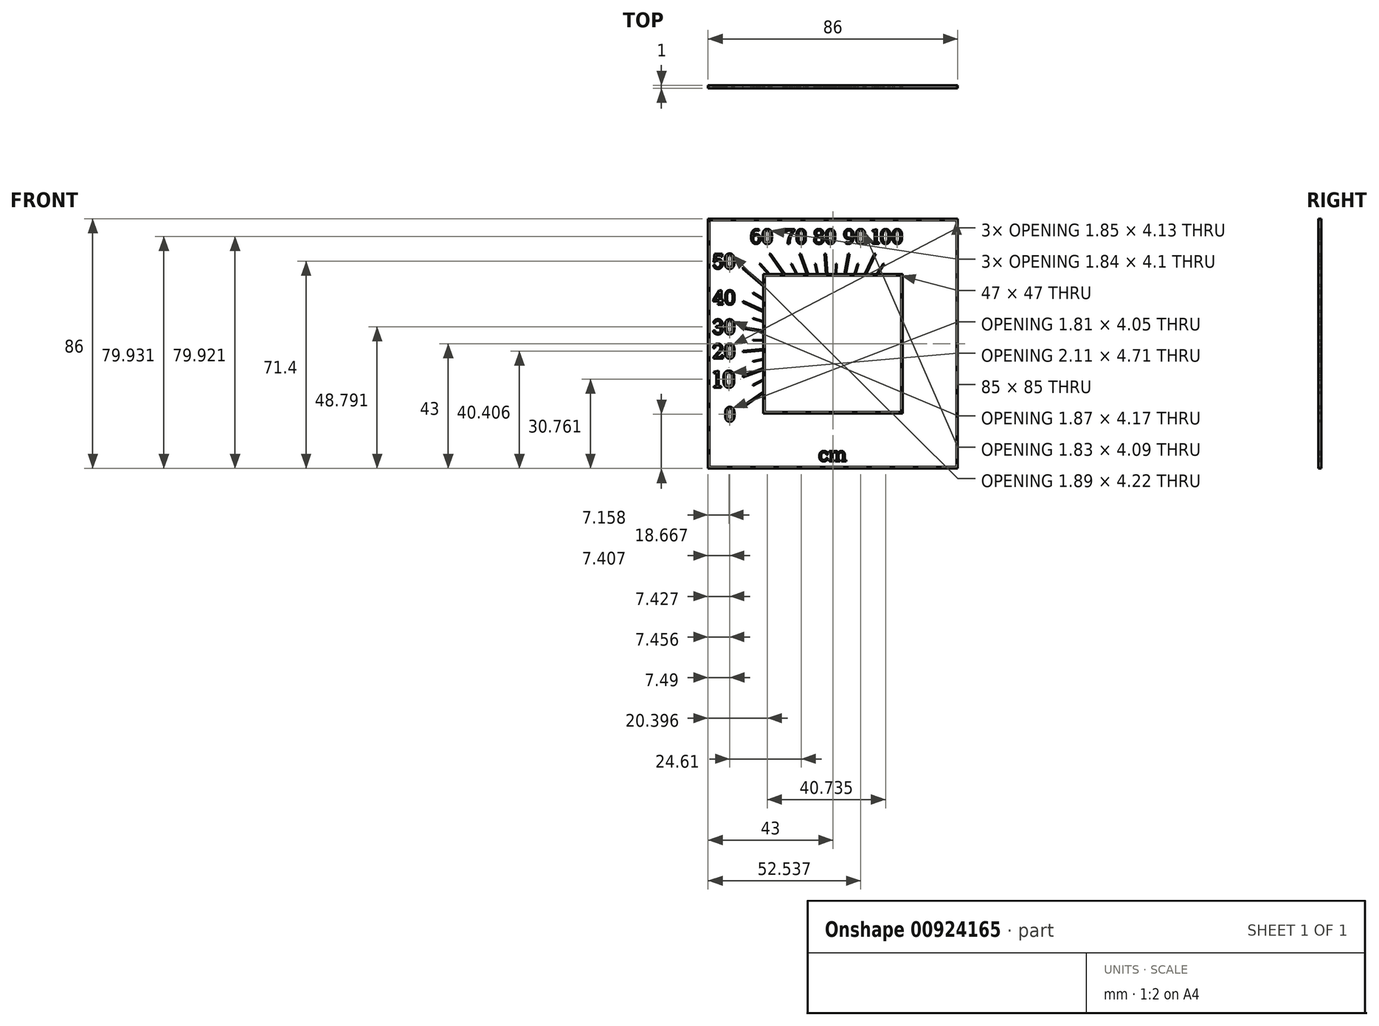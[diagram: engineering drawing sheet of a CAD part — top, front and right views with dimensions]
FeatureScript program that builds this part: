
annotation { "Feature Type Name" : "Feature", "Feature Type Description" : "" }
export const myFeature = defineFeature(function(context is Context, id is Id, definition is map)
    precondition{}
    {
        {
            var Q0;
            Q0=qCreatedBy(makeId("Front.planeOp"),FACE);
            var sketch = newSketch(context, id + "F0", { "sketchPlane" : qUnion([Q0])});
            skLineSegment(sketch, "E0.bottom", {"start": v(-24, 24) * mm, "end": v(-16.8, 24) * mm});
            skLineSegment(sketch, "E0.top", {"start": v(-24, -24) * mm, "end": v(24, -24) * mm});
            skLineSegment(sketch, "E0.left", {"start": v(-24, 24) * mm, "end": v(-24, 11.13) * mm});
            skLineSegment(sketch, "E0.right", {"start": v(24, 24) * mm, "end": v(24, -24) * mm});
            skLineSegment(sketch, "E1.bottom", {"start": v(42.5, -42.5) * mm, "end": v(-42.5, -42.5) * mm});
            skLineSegment(sketch, "E1.top", {"start": v(42.5, 42.5) * mm, "end": v(-42.5, 42.5) * mm});
            skLineSegment(sketch, "E1.left", {"start": v(42.5, -42.5) * mm, "end": v(42.5, 42.5) * mm});
            skLineSegment(sketch, "E1.right", {"start": v(-42.5, -42.5) * mm, "end": v(-42.5, 42.5) * mm});
            skPoint(sketch, "E1.middle", {"position": v(0, 0) * mm});
            skLineSegment(sketch, "E2", {"start": v(0, 0) * mm, "end": v(-29, -20.3) * mm});
            skLineSegment(sketch, "E3.1.0", {"start": v(0, 0) * mm, "end": v(-24, -8.74) * mm, "construction": true});
            skLineSegment(sketch, "E3.2.0", {"start": v(0, 0) * mm, "end": v(-24, -2.1) * mm, "construction": true});
            skLineSegment(sketch, "E3.3.0", {"start": v(0, 0) * mm, "end": v(-24, 4.23) * mm, "construction": true});
            skLineSegment(sketch, "E3.4.0", {"start": v(0, 0) * mm, "end": v(-24, 11.2) * mm, "construction": true});
            skLineSegment(sketch, "E3.5.0", {"start": v(0, 0) * mm, "end": v(-24, 20.14) * mm, "construction": true});
            skLineSegment(sketch, "E3.6.0", {"start": v(0, 0) * mm, "end": v(-20.3, 29) * mm});
            skLineSegment(sketch, "E3.7.0", {"start": v(0, 0) * mm, "end": v(-8.74, 24) * mm, "construction": true});
            skLineSegment(sketch, "E3.8.0", {"start": v(0, 0) * mm, "end": v(-2.1, 24) * mm, "construction": true});
            skLineSegment(sketch, "E3.9.0", {"start": v(0, 0) * mm, "end": v(4.23, 24) * mm, "construction": true});
            skLineSegment(sketch, "E3.10.0", {"start": v(0, 0) * mm, "end": v(14.46, 31) * mm});
            skLineSegment(sketch, "E3.anchor1", {"start": v(0, 0) * mm, "end": v(-24, -16.8) * mm, "construction": true});
            skLineSegment(sketch, "E3.anchor2", {"start": v(0, 0) * mm, "end": v(11.2, 24) * mm, "construction": true});
            skText(sketch, "E4", { "text": "0", "fontName": "RobotoSlab-Regular.ttf"});
            skText(sketch, "E5", { "text": "10", "fontName": "RobotoSlab-Regular.ttf"});
            skText(sketch, "E6", { "text": "20", "fontName": "RobotoSlab-Regular.ttf"});
            skText(sketch, "E7", { "text": "30", "fontName": "RobotoSlab-Regular.ttf"});
            skText(sketch, "E8", { "text": "40", "fontName": "RobotoSlab-Regular.ttf"});
            skText(sketch, "E9", { "text": "50", "fontName": "RobotoSlab-Regular.ttf"});
            skText(sketch, "E10", { "text": "60", "fontName": "RobotoSlab-Regular.ttf"});
            skText(sketch, "E11", { "text": "70", "fontName": "RobotoSlab-Regular.ttf"});
            skText(sketch, "E12", { "text": "80", "fontName": "RobotoSlab-Regular.ttf"});
            skText(sketch, "E13", { "text": "90", "fontName": "RobotoSlab-Regular.ttf"});
            skText(sketch, "E14", { "text": "100", "fontName": "RobotoSlab-Regular.ttf"});
            skLineSegment(sketch, "E15", {"start": v(-41.5, 33.62) * mm, "end": v(-41.5, -35.39) * mm, "construction": true});
            skLineSegment(sketch, "E16.bottom", {"start": v(31, -31) * mm, "end": v(-31, -31) * mm, "construction": true});
            skLineSegment(sketch, "E16.top", {"start": v(31, 31) * mm, "end": v(-31, 31) * mm, "construction": true});
            skLineSegment(sketch, "E16.left", {"start": v(31, -31) * mm, "end": v(31, 31) * mm, "construction": true});
            skLineSegment(sketch, "E16.right", {"start": v(-31, -31) * mm, "end": v(-31, -21.7) * mm, "construction": true});
            skLineSegment(sketch, "E17", {"start": v(-42.5, 39.5) * mm, "end": v(42.5, 39.5) * mm, "construction": true});
            skLineSegment(sketch, "E18", {"start": v(-31, -21.7) * mm, "end": v(-31, -11.28) * mm, "construction": true});
            skLineSegment(sketch, "E19", {"start": v(-31, -11.28) * mm, "end": v(-31, 31) * mm, "construction": true});
            skLineSegment(sketch, "E20", {"start": v(-24, -8.74) * mm, "end": v(-29, -10.56) * mm});
            skLineSegment(sketch, "E21", {"start": v(-24, -2.1) * mm, "end": v(-24, -24) * mm});
            skLineSegment(sketch, "E22", {"start": v(-24, 4.23) * mm, "end": v(-31, 5.47) * mm});
            skLineSegment(sketch, "E23", {"start": v(-24, 11.13) * mm, "end": v(-24, -2.1) * mm});
            skLineSegment(sketch, "E24", {"start": v(-31, 5.47) * mm, "end": v(-31, 5.47) * mm});
            skLineSegment(sketch, "E25", {"start": v(-24, -16.8) * mm, "end": v(-31, -21.7) * mm});
            skLineSegment(sketch, "E26", {"start": v(-24, 11.2) * mm, "end": v(-31, 14.46) * mm});
            skLineSegment(sketch, "E27", {"start": v(-24, -2.1) * mm, "end": v(-31, -2.71) * mm});
            skPoint(sketch, "E28.orphan", {"position": v(-27.12, 22.76) * mm});
            skLineSegment(sketch, "E29", {"start": v(-24, 20.14) * mm, "end": v(-31, 26.01) * mm});
            skLineSegment(sketch, "E30", {"start": v(-16.8, 24) * mm, "end": v(24, 24) * mm});
            skLineSegment(sketch, "E31", {"start": v(-8.74, 24) * mm, "end": v(-11.28, 31) * mm});
            skLineSegment(sketch, "E32", {"start": v(-2.1, 24) * mm, "end": v(-2.71, 31) * mm});
            skLineSegment(sketch, "E33", {"start": v(4.23, 24) * mm, "end": v(5.47, 31) * mm});
            skLineSegment(sketch, "E34", {"start": v(11.2, 24) * mm, "end": v(14.46, 31) * mm, "construction": true});
            skLineSegment(sketch, "E35.bottom", {"start": v(-11.55, 31) * mm, "end": v(-11.02, 31) * mm});
            skLineSegment(sketch, "E35.top", {"start": v(-9, 24) * mm, "end": v(-8.47, 24) * mm});
            skLineSegment(sketch, "E35.left", {"start": v(-11.55, 31) * mm, "end": v(-9, 24) * mm});
            skLineSegment(sketch, "E35.right", {"start": v(-11.02, 31) * mm, "end": v(-8.47, 24) * mm});
            skLineSegment(sketch, "E36.bottom", {"start": v(-22.01, 31) * mm, "end": v(-21.4, 31) * mm});
            skLineSegment(sketch, "E36.top", {"start": v(-17.1, 23.99) * mm, "end": v(-16.5, 23.99) * mm});
            skLineSegment(sketch, "E36.left", {"start": v(-22.01, 31) * mm, "end": v(-17.1, 23.99) * mm});
            skLineSegment(sketch, "E36.right", {"start": v(-21.4, 31) * mm, "end": v(-16.5, 23.99) * mm});
            skLineSegment(sketch, "E37.bottom", {"start": v(-31, -21.4) * mm, "end": v(-24, -16.5) * mm});
            skLineSegment(sketch, "E37.top", {"start": v(-31, -22.01) * mm, "end": v(-24, -17.11) * mm});
            skLineSegment(sketch, "E37.left", {"start": v(-31, -21.4) * mm, "end": v(-31, -22.01) * mm});
            skLineSegment(sketch, "E37.right", {"start": v(-24, -16.5) * mm, "end": v(-24, -17.11) * mm});
            skLineSegment(sketch, "E38.bottom", {"start": v(-31, -11.02) * mm, "end": v(-24, -8.47) * mm});
            skLineSegment(sketch, "E38.top", {"start": v(-31, -11.55) * mm, "end": v(-24, -9) * mm});
            skLineSegment(sketch, "E38.left", {"start": v(-31, -11.02) * mm, "end": v(-31, -11.55) * mm});
            skLineSegment(sketch, "E38.right", {"start": v(-24, -8.47) * mm, "end": v(-24, -9) * mm});
            skLineSegment(sketch, "E39", {"start": v(-31, -2.46) * mm, "end": v(-24, -1.85) * mm});
            skLineSegment(sketch, "E40", {"start": v(-24, -1.85) * mm, "end": v(-24, -2.35) * mm});
            skLineSegment(sketch, "E41", {"start": v(-24, -2.35) * mm, "end": v(-31, -2.96) * mm});
            skLineSegment(sketch, "E42", {"start": v(-31, -2.96) * mm, "end": v(-31, -2.46) * mm});
            skLineSegment(sketch, "E43", {"start": v(-31, 5.21) * mm, "end": v(-31, 5.72) * mm});
            skLineSegment(sketch, "E44", {"start": v(-31, 5.72) * mm, "end": v(-24, 4.49) * mm});
            skLineSegment(sketch, "E45", {"start": v(-24, 4.49) * mm, "end": v(-24, 3.98) * mm});
            skLineSegment(sketch, "E46", {"start": v(-24, 3.98) * mm, "end": v(-31, 5.21) * mm});
            skLineSegment(sketch, "E47", {"start": v(-31, 14.18) * mm, "end": v(-31, 14.73) * mm});
            skLineSegment(sketch, "E48", {"start": v(-31, 14.73) * mm, "end": v(-24, 11.47) * mm});
            skLineSegment(sketch, "E49", {"start": v(-24, 11.47) * mm, "end": v(-24, 10.92) * mm});
            skLineSegment(sketch, "E50", {"start": v(-24, 10.92) * mm, "end": v(-31, 14.18) * mm});
            skLineSegment(sketch, "E51", {"start": v(-31, 25.69) * mm, "end": v(-31, 26.34) * mm});
            skLineSegment(sketch, "E52", {"start": v(-31, 26.34) * mm, "end": v(-24, 20.46) * mm});
            skLineSegment(sketch, "E53", {"start": v(-24, 20.46) * mm, "end": v(-24, 19.81) * mm});
            skLineSegment(sketch, "E54", {"start": v(-24, 19.81) * mm, "end": v(-31, 25.69) * mm});
            skLineSegment(sketch, "E55", {"start": v(-2.96, 31) * mm, "end": v(-2.46, 31) * mm});
            skLineSegment(sketch, "E56", {"start": v(-2.35, 24) * mm, "end": v(-2.96, 31) * mm});
            skLineSegment(sketch, "E57", {"start": v(-2.46, 31) * mm, "end": v(-1.85, 24) * mm});
            skLineSegment(sketch, "E58", {"start": v(-2.35, 24) * mm, "end": v(-1.85, 24) * mm});
            skLineSegment(sketch, "E59", {"start": v(5.21, 31) * mm, "end": v(5.72, 31) * mm});
            skLineSegment(sketch, "E60", {"start": v(5.72, 31) * mm, "end": v(4.49, 24) * mm});
            skLineSegment(sketch, "E61", {"start": v(4.49, 24) * mm, "end": v(3.98, 24) * mm});
            skLineSegment(sketch, "E62", {"start": v(3.98, 24) * mm, "end": v(5.21, 31) * mm});
            skLineSegment(sketch, "E63", {"start": v(14.18, 31) * mm, "end": v(14.73, 31) * mm});
            skLineSegment(sketch, "E64", {"start": v(14.73, 31) * mm, "end": v(11.47, 24) * mm});
            skLineSegment(sketch, "E65", {"start": v(11.47, 24) * mm, "end": v(10.92, 24) * mm});
            skLineSegment(sketch, "E66", {"start": v(10.92, 24) * mm, "end": v(14.18, 31) * mm});
            skLineSegment(sketch, "E67.bottom", {"start": v(43, -43) * mm, "end": v(-43, -43) * mm});
            skLineSegment(sketch, "E67.top", {"start": v(43, 43) * mm, "end": v(-43, 43) * mm});
            skLineSegment(sketch, "E67.left", {"start": v(43, -43) * mm, "end": v(43, 43) * mm});
            skLineSegment(sketch, "E67.right", {"start": v(-43, -43) * mm, "end": v(-43, 43) * mm});
            skLineSegment(sketch, "E68.bottom", {"start": v(23.5, -23.5) * mm, "end": v(-23.5, -23.5) * mm});
            skLineSegment(sketch, "E68.top", {"start": v(23.5, 23.5) * mm, "end": v(-23.5, 23.5) * mm});
            skLineSegment(sketch, "E68.left", {"start": v(23.5, -23.5) * mm, "end": v(23.5, 23.5) * mm});
            skLineSegment(sketch, "E68.right", {"start": v(-23.5, -23.5) * mm, "end": v(-23.5, 23.5) * mm});
            const initialGuessF0  = {"E4": [-0.0375, -0.02681, 1, 0, 0.00502], "E5": [-0.0415, -0.01512, 1, 0, 0.00584], "E6": [-0.0415, -0.00512, 1, 0, 0.00512], "E7": [-0.0415, 0.00324, 1, 0, 0.00517], "E8": [-0.0415, 0.01343, 1, 0, 0.005], "E9": [-0.0415, 0.02582, 1, 0, 0.00523], "E10": [-0.02857, 0.03441, 1, 0, 0.00509], "E11": [-0.01688, 0.03438, 1, 0, 0.00512], "E12": [-0.00681, 0.03438, 1, 0, 0.00512], "E13": [0.00356, 0.03443, 1, 0, 0.00507], "E14": [0.0132, 0.03441, 1, 0, 0.00509]};
            skSetInitialGuess(sketch, initialGuessF0);
            skSolve(sketch);
        }
        {
            var Q0;
            Q0=makeQuery(id+"F0.imprint","IMPRINT",FACE,{"disambiguationData":[TD([[makeQuery(id+"F0.imprint","IMPRINT",EDGE,{"derivedFrom":sQuery(id+"F0.wireOp",EDGE,"E10.sketch_text.stroke-28")}),-1.0]])]});
            var Q1;
            Q1=makeQuery(id+"F0.imprint","IMPRINT",FACE,{"disambiguationData":[TD([[makeQuery(id+"F0.imprint","IMPRINT",EDGE,{"derivedFrom":sQuery(id+"F0.wireOp",EDGE,"E12.sketch_text.stroke-32")}),-1.0]])]});
            var Q2;
            Q2=makeQuery(id+"F0.imprint","IMPRINT",FACE,{"disambiguationData":[TD([[makeQuery(id+"F0.imprint","IMPRINT",EDGE,{"derivedFrom":sQuery(id+"F0.wireOp",EDGE,"E14.sketch_text.stroke-0")}),-1.0]])]});
            var Q3;
            Q3=makeQuery(id+"F0.imprint","IMPRINT",FACE,{"disambiguationData":[TD([[makeQuery(id+"F0.imprint","IMPRINT",EDGE,{"derivedFrom":sQuery(id+"F0.wireOp",EDGE,"E13.sketch_text.stroke-0")}),-1.0]])]});
            var Q4;
            Q4=makeQuery(id+"F0.imprint","IMPRINT",FACE,{"disambiguationData":[TD([[makeQuery(id+"F0.imprint","IMPRINT",EDGE,{"derivedFrom":sQuery(id+"F0.wireOp",EDGE,"E11.sketch_text.stroke-0")}),-1.0]])]});
            var Q5;
            Q5=makeQuery(id+"F0.imprint","IMPRINT",FACE,{"disambiguationData":[TD([[makeQuery(id+"F0.imprint","IMPRINT",EDGE,{"derivedFrom":sQuery(id+"F0.wireOp",EDGE,"E14.sketch_text.stroke-30")}),-1.0]])]});
            var Q6;
            Q6=makeQuery(id+"F0.imprint","IMPRINT",FACE,{"disambiguationData":[TD([[makeQuery(id+"F0.imprint","IMPRINT",EDGE,{"derivedFrom":sQuery(id+"F0.wireOp",EDGE,"E8.sketch_text.stroke-0")}),-1.0]])]});
            var Q7;
            Q7=makeQuery(id+"F0.imprint","IMPRINT",FACE,{"disambiguationData":[TD([[makeQuery(id+"F0.imprint","IMPRINT",EDGE,{"derivedFrom":sQuery(id+"F0.wireOp",EDGE,"E5.sketch_text.stroke-0")}),-1.0]])]});
            var Q8;
            Q8=makeQuery(id+"F0.imprint","IMPRINT",FACE,{"disambiguationData":[TD([[makeQuery(id+"F0.imprint","IMPRINT",EDGE,{"derivedFrom":sQuery(id+"F0.wireOp",EDGE,"E10.sketch_text.stroke-0")}),-1.0]])]});
            var Q9;
            Q9=makeQuery(id+"F0.imprint","IMPRINT",FACE,{"disambiguationData":[TD([[makeQuery(id+"F0.imprint","IMPRINT",EDGE,{"derivedFrom":sQuery(id+"F0.wireOp",EDGE,"E14.sketch_text.stroke-10")}),-1.0]])]});
            var Q10;
            Q10=makeQuery(id+"F0.imprint","IMPRINT",FACE,{"disambiguationData":[TD([[makeQuery(id+"F0.imprint","IMPRINT",EDGE,{"derivedFrom":sQuery(id+"F0.wireOp",EDGE,"E7.sketch_text.stroke-0")}),-1.0]])]});
            var Q11;
            Q11=makeQuery(id+"F0.imprint","IMPRINT",FACE,{"disambiguationData":[TD([[makeQuery(id+"F0.imprint","IMPRINT",EDGE,{"derivedFrom":sQuery(id+"F0.wireOp",EDGE,"E12.sketch_text.stroke-0")}),-1.0]])]});
            var Q12;
            {var subQ10=sQuery(id+"F0.wireOp",EDGE,"E0.top");Q12=makeQuery(id+"F0.imprint","IMPRINT",FACE,{"disambiguationData":[TD([[makeQuery(id+"F0.imprint","IMPRINT",EDGE,{"derivedFrom":subQ10}),1.0]])]});}
            var Q13;
            {var subQ2=sQuery(id+"F0.wireOp",EDGE,"E38.bottom");Q13=makeQuery(id+"F0.imprint","IMPRINT",FACE,{"disambiguationData":[TD([[makeQuery(id+"F0.imprint","IMPRINT",EDGE,{"derivedFrom":subQ2}),-1.0]])]});}
            var Q14;
            {var subQ0=sQuery(id+"F0.wireOp",EDGE,"E27");Q14=makeQuery(id+"F0.imprint","IMPRINT",FACE,{"disambiguationData":[TD([[makeQuery(id+"F0.imprint","IMPRINT",EDGE,{"derivedFrom":subQ0}),-1.0]])]});}
            var Q15;
            Q15=makeQuery(id+"F0.imprint","IMPRINT",FACE,{"disambiguationData":[TD([[makeQuery(id+"F0.imprint","IMPRINT",EDGE,{"derivedFrom":sQuery(id+"F0.wireOp",EDGE,"E9.sketch_text.stroke-0")}),-1.0]])]});
            var Q16;
            Q16=makeQuery(id+"F0.imprint","IMPRINT",FACE,{"disambiguationData":[TD([[makeQuery(id+"F0.imprint","IMPRINT",EDGE,{"derivedFrom":sQuery(id+"F0.wireOp",EDGE,"E4.sketch_text.stroke-0")}),-1.0]])]});
            var Q17;
            {var subQ0=sQuery(id+"F0.wireOp",EDGE,"E33");Q17=makeQuery(id+"F0.imprint","IMPRINT",FACE,{"disambiguationData":[TD([[makeQuery(id+"F0.imprint","IMPRINT",EDGE,{"derivedFrom":subQ0}),-1.0]])]});}
            var Q18;
            {var subQ0=sQuery(id+"F0.wireOp",EDGE,"E29");Q18=makeQuery(id+"F0.imprint","IMPRINT",FACE,{"disambiguationData":[TD([[makeQuery(id+"F0.imprint","IMPRINT",EDGE,{"derivedFrom":subQ0}),-1.0]])]});}
            var Q19;
            {var subQ0=sQuery(id+"F0.wireOp",EDGE,"E37.top");Q19=makeQuery(id+"F0.imprint","IMPRINT",FACE,{"disambiguationData":[TD([[makeQuery(id+"F0.imprint","IMPRINT",EDGE,{"derivedFrom":subQ0}),1.0]])]});}
            var Q20;
            {var subQ1=sQuery(id+"F0.wireOp",EDGE,"E36.bottom");Q20=makeQuery(id+"F0.imprint","IMPRINT",FACE,{"disambiguationData":[TD([[makeQuery(id+"F0.imprint","IMPRINT",EDGE,{"derivedFrom":subQ1}),-1.0]])]});}
            var Q21;
            {var subQ0=sQuery(id+"F0.wireOp",EDGE,"E33");Q21=makeQuery(id+"F0.imprint","IMPRINT",FACE,{"disambiguationData":[TD([[makeQuery(id+"F0.imprint","IMPRINT",EDGE,{"derivedFrom":subQ0}),1.0]])]});}
            var Q22;
            {var subQ0=sQuery(id+"F0.wireOp",EDGE,"E26");Q22=makeQuery(id+"F0.imprint","IMPRINT",FACE,{"disambiguationData":[TD([[makeQuery(id+"F0.imprint","IMPRINT",EDGE,{"derivedFrom":subQ0}),-1.0]])]});}
            var Q23;
            Q23=makeQuery(id+"F0.imprint","IMPRINT",FACE,{"disambiguationData":[TD([[makeQuery(id+"F0.imprint","IMPRINT",EDGE,{"derivedFrom":sQuery(id+"F0.wireOp",EDGE,"E5.sketch_text.stroke-10")}),-1.0]])]});
            var Q24;
            {var subQ0=sQuery(id+"F0.wireOp",EDGE,"E29");Q24=makeQuery(id+"F0.imprint","IMPRINT",FACE,{"disambiguationData":[TD([[makeQuery(id+"F0.imprint","IMPRINT",EDGE,{"derivedFrom":subQ0}),1.0]])]});}
            var Q25;
            {var subQ0=sQuery(id+"F0.wireOp",EDGE,"E27");Q25=makeQuery(id+"F0.imprint","IMPRINT",FACE,{"disambiguationData":[TD([[makeQuery(id+"F0.imprint","IMPRINT",EDGE,{"derivedFrom":subQ0}),1.0]])]});}
            var Q26;
            Q26=makeQuery(id+"F0.imprint","IMPRINT",FACE,{"disambiguationData":[TD([[makeQuery(id+"F0.imprint","IMPRINT",EDGE,{"derivedFrom":sQuery(id+"F0.wireOp",EDGE,"E9.sketch_text.stroke-26")}),-1.0]])]});
            var Q27;
            Q27=makeQuery(id+"F0.imprint","IMPRINT",FACE,{"disambiguationData":[TD([[makeQuery(id+"F0.imprint","IMPRINT",EDGE,{"derivedFrom":sQuery(id+"F0.wireOp",EDGE,"E8.sketch_text.stroke-20")}),-1.0]])]});
            var Q28;
            {var subQ0=sQuery(id+"F0.wireOp",EDGE,"E31");Q28=makeQuery(id+"F0.imprint","IMPRINT",FACE,{"disambiguationData":[TD([[makeQuery(id+"F0.imprint","IMPRINT",EDGE,{"derivedFrom":subQ0}),-1.0]])]});}
            var Q29;
            {var subQ0=sQuery(id+"F0.wireOp",EDGE,"E32");Q29=makeQuery(id+"F0.imprint","IMPRINT",FACE,{"disambiguationData":[TD([[makeQuery(id+"F0.imprint","IMPRINT",EDGE,{"derivedFrom":subQ0}),1.0]])]});}
            var Q30;
            Q30=makeQuery(id+"F0.imprint","IMPRINT",FACE,{"disambiguationData":[TD([[makeQuery(id+"F0.imprint","IMPRINT",EDGE,{"derivedFrom":sQuery(id+"F0.wireOp",EDGE,"E6.sketch_text.stroke-0")}),-1.0]])]});
            var Q31;
            {var subQ0=sQuery(id+"F0.wireOp",EDGE,"E22");Q31=makeQuery(id+"F0.imprint","IMPRINT",FACE,{"disambiguationData":[TD([[makeQuery(id+"F0.imprint","IMPRINT",EDGE,{"derivedFrom":subQ0}),1.0]])]});}
            var Q32;
            {var subQ0=sQuery(id+"F0.wireOp",EDGE,"E32");Q32=makeQuery(id+"F0.imprint","IMPRINT",FACE,{"disambiguationData":[TD([[makeQuery(id+"F0.imprint","IMPRINT",EDGE,{"derivedFrom":subQ0}),-1.0]])]});}
            var Q33;
            {var subQ5=sQuery(id+"F0.wireOp",EDGE,"E64");Q33=makeQuery(id+"F0.imprint","IMPRINT",FACE,{"disambiguationData":[TD([[makeQuery(id+"F0.imprint","IMPRINT",EDGE,{"derivedFrom":subQ5}),-1.0]])]});}
            var Q34;
            Q34=makeQuery(id+"F0.imprint","IMPRINT",FACE,{"disambiguationData":[TD([[makeQuery(id+"F0.imprint","IMPRINT",EDGE,{"derivedFrom":sQuery(id+"F0.wireOp",EDGE,"E11.sketch_text.stroke-13")}),-1.0]])]});
            var Q35;
            {var subQ1=sQuery(id+"F0.wireOp",EDGE,"E0.left");var subQ33=sQuery(id+"F0.wireOp",EDGE,"E0.bottom");var subQ35=makeQuery(id+"F0.imprint","INTERSECT",VERTEX,{"derivedFrom":[subQ33,subQ1]});Q35=makeQuery(id+"F0.imprint","IMPRINT",FACE,{"disambiguationData":[TD([[makeQuery(id+"F0.imprint","IMPRINT",EDGE,{"disambiguationData":[TD([[subQ35,-1.0]])],"derivedFrom":subQ33}),-1.0]])]});}
            var Q36;
            {var subQ0=sQuery(id+"F0.wireOp",EDGE,"E26");Q36=makeQuery(id+"F0.imprint","IMPRINT",FACE,{"disambiguationData":[TD([[makeQuery(id+"F0.imprint","IMPRINT",EDGE,{"derivedFrom":subQ0}),1.0]])]});}
            var Q37;
            {var subQ0=sQuery(id+"F0.wireOp",EDGE,"E22");Q37=makeQuery(id+"F0.imprint","IMPRINT",FACE,{"disambiguationData":[TD([[makeQuery(id+"F0.imprint","IMPRINT",EDGE,{"derivedFrom":subQ0}),-1.0]])]});}
            var Q38;
            Q38=makeQuery(id+"F0.imprint","IMPRINT",FACE,{"disambiguationData":[TD([[makeQuery(id+"F0.imprint","IMPRINT",EDGE,{"derivedFrom":sQuery(id+"F0.wireOp",EDGE,"E7.sketch_text.stroke-31")}),-1.0]])]});
            var Q39;
            {var subQ0=sQuery(id+"F0.wireOp",EDGE,"E31");Q39=makeQuery(id+"F0.imprint","IMPRINT",FACE,{"disambiguationData":[TD([[makeQuery(id+"F0.imprint","IMPRINT",EDGE,{"derivedFrom":subQ0}),1.0]])]});}
            var Q40;
            Q40=makeQuery(id+"F0.imprint","IMPRINT",FACE,{"disambiguationData":[TD([[makeQuery(id+"F0.imprint","IMPRINT",EDGE,{"derivedFrom":sQuery(id+"F0.wireOp",EDGE,"E6.sketch_text.stroke-23")}),-1.0]])]});
            var Q41;
            Q41=makeQuery(id+"F0.imprint","IMPRINT",FACE,{"disambiguationData":[TD([[makeQuery(id+"F0.imprint","IMPRINT",EDGE,{"derivedFrom":sQuery(id+"F0.wireOp",EDGE,"E13.sketch_text.stroke-28")}),-1.0]])]});
            var Q42;
            {var subQ3=sQuery(id+"F0.wireOp",EDGE,"E3.6.0");var subQ18=sQuery(id+"F0.wireOp",EDGE,"E68.top");var subQ19=makeQuery(id+"F0.imprint","INTERSECT",VERTEX,{"derivedFrom":[subQ3,subQ18]});Q42=makeQuery(id+"F0.imprint","IMPRINT",FACE,{"disambiguationData":[TD([[makeQuery(id+"F0.imprint","IMPRINT",EDGE,{"disambiguationData":[TD([[subQ19,-1.0]])],"derivedFrom":subQ3}),-1.0]])]});}
            var Q43;
            {var subQ5=sQuery(id+"F0.wireOp",EDGE,"E66");Q43=makeQuery(id+"F0.imprint","IMPRINT",FACE,{"disambiguationData":[TD([[makeQuery(id+"F0.imprint","IMPRINT",EDGE,{"derivedFrom":subQ5}),-1.0]])]});}
            var Q44;
            {var subQ3=sQuery(id+"F0.wireOp",EDGE,"E37.bottom");Q44=makeQuery(id+"F0.imprint","IMPRINT",FACE,{"disambiguationData":[TD([[makeQuery(id+"F0.imprint","IMPRINT",EDGE,{"derivedFrom":subQ3}),-1.0]])]});}
            var Q45;
            {var subQ3=sQuery(id+"F0.wireOp",EDGE,"E36.left");var subQ5=sQuery(id+"F0.wireOp",EDGE,"E36.top");var subQ6=makeQuery(id+"F0.imprint","INTERSECT",VERTEX,{"derivedFrom":[subQ5,subQ3]});Q45=makeQuery(id+"F0.imprint","IMPRINT",FACE,{"disambiguationData":[TD([[makeQuery(id+"F0.imprint","IMPRINT",EDGE,{"disambiguationData":[TD([[subQ6,-1.0]])],"derivedFrom":subQ5}),1.0]])]});}
            var Q46;
            {var subQ3=sQuery(id+"F0.wireOp",EDGE,"E36.top");var subQ5=sQuery(id+"F0.wireOp",EDGE,"E36.right");var subQ7=makeQuery(id+"F0.imprint","INTERSECT",VERTEX,{"derivedFrom":[subQ3,subQ5]});Q46=makeQuery(id+"F0.imprint","IMPRINT",FACE,{"disambiguationData":[TD([[makeQuery(id+"F0.imprint","IMPRINT",EDGE,{"disambiguationData":[TD([[subQ7,1.0]])],"derivedFrom":subQ3}),1.0]])]});}
            extrude(context, id + "F1", {"entities" : qUnion([Q0, Q1, Q2, Q3, Q4, Q5, Q6, Q7, Q8, Q9, Q10, Q11, Q12, Q13, Q14, Q15, Q16, Q17, Q18, Q19, Q20, Q21, Q22, Q23, Q24, Q25, Q26, Q27, Q28, Q29, Q30, Q31, Q32, Q33, Q34, Q35, Q36, Q37, Q38, Q39, Q40, Q41, Q42, Q43, Q44, Q45, Q46]), "depth" : 1 * mm, "offsetDistance" : 25 * mm});
        }
        {
            var Q0;
            Q0=qCreatedBy(makeId("Front.planeOp"),FACE);
            var sketch = newSketch(context, id + "F2", { "sketchPlane" : qUnion([Q0])});
            skLineSegment(sketch, "E69.0", {"start": v(0, 0) * mm, "end": v(-29, -20.3) * mm});
            skLineSegment(sketch, "E70.0", {"start": v(0, 0) * mm, "end": v(12.82, 27.5) * mm});
            skLineSegment(sketch, "E71.bottom", {"start": v(24, -24) * mm, "end": v(-24, -24) * mm, "construction": true});
            skLineSegment(sketch, "E71.top", {"start": v(24, 24) * mm, "end": v(-22, 24) * mm, "construction": true});
            skLineSegment(sketch, "E71.left", {"start": v(24, -24) * mm, "end": v(24, 24) * mm, "construction": true});
            skLineSegment(sketch, "E71.right", {"start": v(-24, -24) * mm, "end": v(-24, 24) * mm, "construction": true});
            skPoint(sketch, "E71.middle", {"position": v(0, 0) * mm});
            skLineSegment(sketch, "E72.bottom", {"start": v(27.5, -27.5) * mm, "end": v(-27.5, -27.5) * mm, "construction": true});
            skLineSegment(sketch, "E72.top", {"start": v(27.5, 27.5) * mm, "end": v(-27.5, 27.5) * mm, "construction": true});
            skLineSegment(sketch, "E72.left", {"start": v(27.5, -27.5) * mm, "end": v(27.5, 27.5) * mm, "construction": true});
            skLineSegment(sketch, "E72.right", {"start": v(-27.5, -27.5) * mm, "end": v(-27.5, 27.5) * mm, "construction": true});
            skLineSegment(sketch, "E73", {"start": v(0, 0) * mm, "end": v(-27.5, -14.32) * mm, "construction": true});
            skLineSegment(sketch, "E74.1.0", {"start": v(0, 0) * mm, "end": v(-24, -5.32) * mm});
            skLineSegment(sketch, "E74.2.0", {"start": v(0, 0) * mm, "end": v(-24, 1.05) * mm});
            skLineSegment(sketch, "E74.3.0", {"start": v(0, 0) * mm, "end": v(-24, 7.57) * mm});
            skLineSegment(sketch, "E74.4.0", {"start": v(0, 0) * mm, "end": v(-24, 15.29) * mm});
            skLineSegment(sketch, "E74.5.0", {"start": v(0, 0) * mm, "end": v(-25.2, 27.5) * mm});
            skLineSegment(sketch, "E74.6.0", {"start": v(0, 0) * mm, "end": v(-12.5, 24) * mm});
            skLineSegment(sketch, "E74.7.0", {"start": v(0, 0) * mm, "end": v(-5.32, 24) * mm});
            skLineSegment(sketch, "E74.8.0", {"start": v(0, 0) * mm, "end": v(1.05, 24) * mm});
            skLineSegment(sketch, "E74.9.0", {"start": v(0, 0) * mm, "end": v(7.57, 24) * mm});
            skLineSegment(sketch, "E74.10.0", {"start": v(0, 0) * mm, "end": v(17.52, 27.5) * mm});
            skLineSegment(sketch, "E74.anchor1", {"start": v(0, 0) * mm, "end": v(-24, -12.5) * mm, "construction": true});
            skLineSegment(sketch, "E74.anchor2", {"start": v(0, 0) * mm, "end": v(15.29, 24) * mm, "construction": true});
            skPoint(sketch, "E75.orphan", {"position": v(-20.95, 22.86) * mm});
            skPoint(sketch, "E76.orphan", {"position": v(-26.15, 16.66) * mm});
            skPoint(sketch, "E77.orphan", {"position": v(-29.57, 9.32) * mm});
            skPoint(sketch, "E78.orphan", {"position": v(-30.97, 1.35) * mm});
            skPoint(sketch, "E79.orphan", {"position": v(-30.27, -6.71) * mm});
            skPoint(sketch, "E80.orphan", {"position": v(-14.32, 27.5) * mm});
            skPoint(sketch, "E81.orphan", {"position": v(-6.71, 30.27) * mm});
            skPoint(sketch, "E82.orphan", {"position": v(1.35, 30.97) * mm});
            skPoint(sketch, "E83.orphan", {"position": v(9.32, 29.57) * mm});
            skPoint(sketch, "E84.orphan", {"position": v(14.46, 31) * mm});
            skLineSegment(sketch, "E85", {"start": v(-22, 24) * mm, "end": v(-24, 24) * mm, "construction": true});
            skLineSegment(sketch, "E86", {"start": v(-12.5, 24) * mm, "end": v(-14.32, 27.5) * mm});
            skLineSegment(sketch, "E87", {"start": v(-5.32, 24) * mm, "end": v(-6.1, 27.5) * mm});
            skLineSegment(sketch, "E88", {"start": v(1.05, 24) * mm, "end": v(1.2, 27.5) * mm});
            skLineSegment(sketch, "E89", {"start": v(7.57, 24) * mm, "end": v(8.67, 27.5) * mm});
            skLineSegment(sketch, "E90", {"start": v(15.29, 24) * mm, "end": v(16.66, 26.15) * mm, "construction": true});
            skLineSegment(sketch, "E91", {"start": v(-24, 15.29) * mm, "end": v(-27.5, 17.52) * mm});
            skLineSegment(sketch, "E92", {"start": v(-24, 7.57) * mm, "end": v(-27.5, 8.67) * mm});
            skLineSegment(sketch, "E93", {"start": v(-24, 1.05) * mm, "end": v(-27.5, 1.2) * mm});
            skLineSegment(sketch, "E94", {"start": v(-24, -5.32) * mm, "end": v(-27.5, -6.1) * mm});
            skLineSegment(sketch, "E95", {"start": v(-24, -12.5) * mm, "end": v(-24, -12.5) * mm});
            skLineSegment(sketch, "E96", {"start": v(-24, -12.5) * mm, "end": v(-27.5, -14.32) * mm, "construction": true});
            skLineSegment(sketch, "E97", {"start": v(-27.5, -14.17) * mm, "end": v(-24, -12.35) * mm});
            skLineSegment(sketch, "E98", {"start": v(-24, -12.35) * mm, "end": v(-24, -12.63) * mm});
            skLineSegment(sketch, "E99", {"start": v(-24, -12.63) * mm, "end": v(-27.5, -14.46) * mm});
            skLineSegment(sketch, "E100", {"start": v(-27.5, -14.46) * mm, "end": v(-27.5, -14.17) * mm});
            skLineSegment(sketch, "E101", {"start": v(-27.5, -5.97) * mm, "end": v(-24, -5.2) * mm});
            skLineSegment(sketch, "E102", {"start": v(-24, -5.2) * mm, "end": v(-24, -5.45) * mm});
            skLineSegment(sketch, "E103", {"start": v(-24, -5.45) * mm, "end": v(-27.5, -6.22) * mm});
            skLineSegment(sketch, "E104", {"start": v(-27.5, -6.22) * mm, "end": v(-27.5, -5.97) * mm});
            skLineSegment(sketch, "E105", {"start": v(-27.5, 1.33) * mm, "end": v(-24, 1.17) * mm});
            skLineSegment(sketch, "E106", {"start": v(-24, 1.17) * mm, "end": v(-24, 0.92) * mm});
            skLineSegment(sketch, "E107", {"start": v(-24, 0.92) * mm, "end": v(-27.5, 1.08) * mm});
            skLineSegment(sketch, "E108", {"start": v(-27.5, 1.08) * mm, "end": v(-27.5, 1.33) * mm});
            skLineSegment(sketch, "E109", {"start": v(-27.5, 8.8) * mm, "end": v(-24, 7.7) * mm});
            skLineSegment(sketch, "E110", {"start": v(-24, 7.7) * mm, "end": v(-24, 7.44) * mm});
            skLineSegment(sketch, "E111", {"start": v(-24, 7.44) * mm, "end": v(-27.5, 8.54) * mm});
            skLineSegment(sketch, "E112", {"start": v(-27.5, 8.54) * mm, "end": v(-27.5, 8.8) * mm});
            skLineSegment(sketch, "E113", {"start": v(-27.5, 17.67) * mm, "end": v(-24, 15.44) * mm});
            skLineSegment(sketch, "E114", {"start": v(-24, 15.44) * mm, "end": v(-24, 15.14) * mm});
            skLineSegment(sketch, "E115", {"start": v(-24, 15.14) * mm, "end": v(-27.5, 17.37) * mm});
            skLineSegment(sketch, "E116", {"start": v(-27.5, 17.37) * mm, "end": v(-27.5, 17.67) * mm});
            skLineSegment(sketch, "E117", {"start": v(-25.37, 27.5) * mm, "end": v(-22.16, 24) * mm});
            skLineSegment(sketch, "E118", {"start": v(-22.16, 24) * mm, "end": v(-21.82, 24) * mm});
            skLineSegment(sketch, "E119", {"start": v(-21.82, 24) * mm, "end": v(-25.03, 27.5) * mm});
            skLineSegment(sketch, "E120", {"start": v(-25.03, 27.5) * mm, "end": v(-25.37, 27.5) * mm});
            skLineSegment(sketch, "E121", {"start": v(-14.2, 27.5) * mm, "end": v(-12.37, 24) * mm});
            skLineSegment(sketch, "E122", {"start": v(-12.37, 24) * mm, "end": v(-12.62, 24) * mm});
            skLineSegment(sketch, "E123", {"start": v(-12.62, 24) * mm, "end": v(-14.44, 27.5) * mm});
            skLineSegment(sketch, "E124", {"start": v(-14.44, 27.5) * mm, "end": v(-14.2, 27.5) * mm});
            skLineSegment(sketch, "E125", {"start": v(-5.97, 27.5) * mm, "end": v(-5.2, 24) * mm});
            skLineSegment(sketch, "E126", {"start": v(-5.2, 24) * mm, "end": v(-5.45, 24) * mm});
            skLineSegment(sketch, "E127", {"start": v(-5.45, 24) * mm, "end": v(-6.22, 27.5) * mm});
            skLineSegment(sketch, "E128", {"start": v(-6.22, 27.5) * mm, "end": v(-5.97, 27.5) * mm});
            skLineSegment(sketch, "E129", {"start": v(1.08, 27.5) * mm, "end": v(0.92, 24) * mm});
            skLineSegment(sketch, "E130", {"start": v(0.92, 24) * mm, "end": v(1.17, 24) * mm});
            skLineSegment(sketch, "E131", {"start": v(1.17, 24) * mm, "end": v(1.33, 27.5) * mm});
            skLineSegment(sketch, "E132", {"start": v(1.33, 27.5) * mm, "end": v(1.08, 27.5) * mm});
            skLineSegment(sketch, "E133", {"start": v(8.54, 27.5) * mm, "end": v(7.44, 24) * mm});
            skLineSegment(sketch, "E134", {"start": v(7.44, 24) * mm, "end": v(7.7, 24) * mm});
            skLineSegment(sketch, "E135", {"start": v(7.7, 24) * mm, "end": v(8.8, 27.5) * mm});
            skLineSegment(sketch, "E136", {"start": v(8.8, 27.5) * mm, "end": v(8.54, 27.5) * mm});
            skLineSegment(sketch, "E137", {"start": v(17.37, 27.5) * mm, "end": v(15.14, 24) * mm});
            skLineSegment(sketch, "E138", {"start": v(15.14, 24) * mm, "end": v(15.44, 24) * mm});
            skLineSegment(sketch, "E139", {"start": v(15.44, 24) * mm, "end": v(17.67, 27.5) * mm});
            skLineSegment(sketch, "E140", {"start": v(17.67, 27.5) * mm, "end": v(17.37, 27.5) * mm});
            skLineSegment(sketch, "E141.bottom", {"start": v(42.5, -42.5) * mm, "end": v(-42.5, -42.5) * mm, "construction": true});
            skLineSegment(sketch, "E141.top", {"start": v(42.5, 42.5) * mm, "end": v(-42.5, 42.5) * mm, "construction": true});
            skLineSegment(sketch, "E141.left", {"start": v(42.5, -42.5) * mm, "end": v(42.5, 42.5) * mm, "construction": true});
            skLineSegment(sketch, "E141.right", {"start": v(-42.5, -42.5) * mm, "end": v(-42.5, 42.5) * mm, "construction": true});
            skText(sketch, "E142", { "text": "cm", "fontName": "RobotoSlab-Regular.ttf"});
            const initialGuessF2  = {"E142": [-0.005, -0.0405, 1, 0, 0.00474]};
            skSetInitialGuess(sketch, initialGuessF2);
            skSolve(sketch);
        }
        {
            var Q0;
            Q0 = qSketchRegion(id + "F2", true);
            var Q1;
            Q1=makeQuery(id+"F0.imprint","IMPRINT",FACE,{"disambiguationData":[TD([[makeQuery(id+"F0.imprint","IMPRINT",EDGE,{"derivedFrom":sQuery(id+"F0.wireOp",EDGE,"E1.bottom")}),1.0]])]});
            extrude(context, id + "F3", {"entities" : qUnion([Q0, Q1]), "depth" : 1 * mm, "offsetDistance" : 25 * mm});
        }
    });
